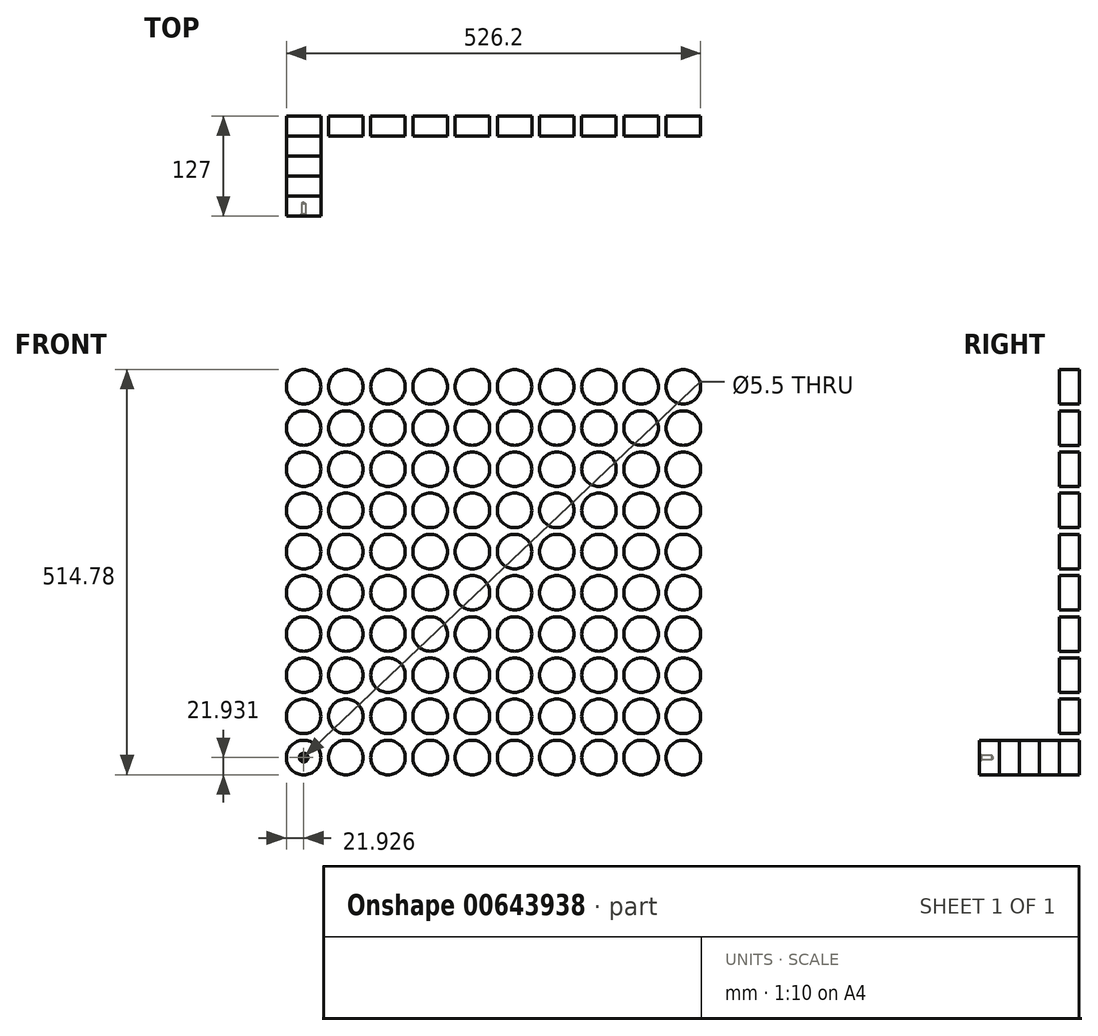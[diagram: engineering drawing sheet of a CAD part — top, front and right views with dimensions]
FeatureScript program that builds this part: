
annotation { "Feature Type Name" : "Feature", "Feature Type Description" : "" }
export const myFeature = defineFeature(function(context is Context, id is Id, definition is map)
    precondition{}
    {
        {
            var Q0;
            Q0=qCreatedBy(makeId("Front.planeOp"),FACE);
            var sketch = newSketch(context, id + "F0", { "sketchPlane" : qUnion([Q0])});
            skCircle(sketch, "E0", {"center": v(-112.8, -47.45) * mm, "radius": 21.93 * mm});
            skCircle(sketch, "E1.0.1.0", {"center": v(-112.8, 4.88) * mm, "radius": 21.93 * mm});
            skCircle(sketch, "E1.0.2.0", {"center": v(-112.8, 57.2) * mm, "radius": 21.93 * mm});
            skCircle(sketch, "E1.0.3.0", {"center": v(-112.8, 109.52) * mm, "radius": 21.93 * mm});
            skCircle(sketch, "E1.0.4.0", {"center": v(-112.8, 161.85) * mm, "radius": 21.93 * mm});
            skCircle(sketch, "E1.0.5.0", {"center": v(-112.8, 214.17) * mm, "radius": 21.93 * mm});
            skCircle(sketch, "E1.0.6.0", {"center": v(-112.8, 266.5) * mm, "radius": 21.93 * mm});
            skCircle(sketch, "E1.0.7.0", {"center": v(-112.8, 318.82) * mm, "radius": 21.93 * mm});
            skCircle(sketch, "E1.0.8.0", {"center": v(-112.8, 371.14) * mm, "radius": 21.93 * mm});
            skCircle(sketch, "E1.0.9.0", {"center": v(-112.8, 423.47) * mm, "radius": 21.93 * mm});
            skCircle(sketch, "E1.1.0.0", {"center": v(-59.2, -47.45) * mm, "radius": 21.93 * mm});
            skCircle(sketch, "E1.1.1.0", {"center": v(-59.2, 4.88) * mm, "radius": 21.93 * mm});
            skCircle(sketch, "E1.1.2.0", {"center": v(-59.2, 57.2) * mm, "radius": 21.93 * mm});
            skCircle(sketch, "E1.1.3.0", {"center": v(-59.2, 109.52) * mm, "radius": 21.93 * mm});
            skCircle(sketch, "E1.1.4.0", {"center": v(-59.2, 161.85) * mm, "radius": 21.93 * mm});
            skCircle(sketch, "E1.1.5.0", {"center": v(-59.2, 214.17) * mm, "radius": 21.93 * mm});
            skCircle(sketch, "E1.1.6.0", {"center": v(-59.2, 266.5) * mm, "radius": 21.93 * mm});
            skCircle(sketch, "E1.1.7.0", {"center": v(-59.2, 318.82) * mm, "radius": 21.93 * mm});
            skCircle(sketch, "E1.1.8.0", {"center": v(-59.2, 371.14) * mm, "radius": 21.93 * mm});
            skCircle(sketch, "E1.1.9.0", {"center": v(-59.2, 423.47) * mm, "radius": 21.93 * mm});
            skCircle(sketch, "E1.2.0.0", {"center": v(-5.62, -47.45) * mm, "radius": 21.93 * mm});
            skCircle(sketch, "E1.2.1.0", {"center": v(-5.62, 4.88) * mm, "radius": 21.93 * mm});
            skCircle(sketch, "E1.2.2.0", {"center": v(-5.62, 57.2) * mm, "radius": 21.93 * mm});
            skCircle(sketch, "E1.2.3.0", {"center": v(-5.62, 109.52) * mm, "radius": 21.93 * mm});
            skCircle(sketch, "E1.2.4.0", {"center": v(-5.62, 161.85) * mm, "radius": 21.93 * mm});
            skCircle(sketch, "E1.2.5.0", {"center": v(-5.62, 214.17) * mm, "radius": 21.93 * mm});
            skCircle(sketch, "E1.2.6.0", {"center": v(-5.62, 266.5) * mm, "radius": 21.93 * mm});
            skCircle(sketch, "E1.2.7.0", {"center": v(-5.62, 318.82) * mm, "radius": 21.93 * mm});
            skCircle(sketch, "E1.2.8.0", {"center": v(-5.62, 371.14) * mm, "radius": 21.93 * mm});
            skCircle(sketch, "E1.2.9.0", {"center": v(-5.62, 423.47) * mm, "radius": 21.93 * mm});
            skCircle(sketch, "E1.3.0.0", {"center": v(47.98, -47.45) * mm, "radius": 21.93 * mm});
            skCircle(sketch, "E1.3.1.0", {"center": v(47.98, 4.88) * mm, "radius": 21.93 * mm});
            skCircle(sketch, "E1.3.2.0", {"center": v(47.98, 57.2) * mm, "radius": 21.93 * mm});
            skCircle(sketch, "E1.3.3.0", {"center": v(47.98, 109.52) * mm, "radius": 21.93 * mm});
            skCircle(sketch, "E1.3.4.0", {"center": v(47.98, 161.85) * mm, "radius": 21.93 * mm});
            skCircle(sketch, "E1.3.5.0", {"center": v(47.98, 214.17) * mm, "radius": 21.93 * mm});
            skCircle(sketch, "E1.3.6.0", {"center": v(47.98, 266.5) * mm, "radius": 21.93 * mm});
            skCircle(sketch, "E1.3.7.0", {"center": v(47.98, 318.82) * mm, "radius": 21.93 * mm});
            skCircle(sketch, "E1.3.8.0", {"center": v(47.98, 371.14) * mm, "radius": 21.93 * mm});
            skCircle(sketch, "E1.3.9.0", {"center": v(47.98, 423.47) * mm, "radius": 21.93 * mm});
            skCircle(sketch, "E1.4.0.0", {"center": v(101.57, -47.45) * mm, "radius": 21.93 * mm});
            skCircle(sketch, "E1.4.1.0", {"center": v(101.57, 4.88) * mm, "radius": 21.93 * mm});
            skCircle(sketch, "E1.4.2.0", {"center": v(101.57, 57.2) * mm, "radius": 21.93 * mm});
            skCircle(sketch, "E1.4.3.0", {"center": v(101.57, 109.52) * mm, "radius": 21.93 * mm});
            skCircle(sketch, "E1.4.4.0", {"center": v(101.57, 161.85) * mm, "radius": 21.93 * mm});
            skCircle(sketch, "E1.4.5.0", {"center": v(101.57, 214.17) * mm, "radius": 21.93 * mm});
            skCircle(sketch, "E1.4.6.0", {"center": v(101.57, 266.5) * mm, "radius": 21.93 * mm});
            skCircle(sketch, "E1.4.7.0", {"center": v(101.57, 318.82) * mm, "radius": 21.93 * mm});
            skCircle(sketch, "E1.4.8.0", {"center": v(101.57, 371.14) * mm, "radius": 21.93 * mm});
            skCircle(sketch, "E1.4.9.0", {"center": v(101.57, 423.47) * mm, "radius": 21.93 * mm});
            skCircle(sketch, "E1.5.0.0", {"center": v(155.17, -47.45) * mm, "radius": 21.93 * mm});
            skCircle(sketch, "E1.5.1.0", {"center": v(155.17, 4.88) * mm, "radius": 21.93 * mm});
            skCircle(sketch, "E1.5.2.0", {"center": v(155.17, 57.2) * mm, "radius": 21.93 * mm});
            skCircle(sketch, "E1.5.3.0", {"center": v(155.17, 109.52) * mm, "radius": 21.93 * mm});
            skCircle(sketch, "E1.5.4.0", {"center": v(155.17, 161.85) * mm, "radius": 21.93 * mm});
            skCircle(sketch, "E1.5.5.0", {"center": v(155.17, 214.17) * mm, "radius": 21.93 * mm});
            skCircle(sketch, "E1.5.6.0", {"center": v(155.17, 266.5) * mm, "radius": 21.93 * mm});
            skCircle(sketch, "E1.5.7.0", {"center": v(155.17, 318.82) * mm, "radius": 21.93 * mm});
            skCircle(sketch, "E1.5.8.0", {"center": v(155.17, 371.14) * mm, "radius": 21.93 * mm});
            skCircle(sketch, "E1.5.9.0", {"center": v(155.17, 423.47) * mm, "radius": 21.93 * mm});
            skCircle(sketch, "E1.6.0.0", {"center": v(208.76, -47.45) * mm, "radius": 21.93 * mm});
            skCircle(sketch, "E1.6.1.0", {"center": v(208.76, 4.88) * mm, "radius": 21.93 * mm});
            skCircle(sketch, "E1.6.2.0", {"center": v(208.76, 57.2) * mm, "radius": 21.93 * mm});
            skCircle(sketch, "E1.6.3.0", {"center": v(208.76, 109.52) * mm, "radius": 21.93 * mm});
            skCircle(sketch, "E1.6.4.0", {"center": v(208.76, 161.85) * mm, "radius": 21.93 * mm});
            skCircle(sketch, "E1.6.5.0", {"center": v(208.76, 214.17) * mm, "radius": 21.93 * mm});
            skCircle(sketch, "E1.6.6.0", {"center": v(208.76, 266.5) * mm, "radius": 21.93 * mm});
            skCircle(sketch, "E1.6.7.0", {"center": v(208.76, 318.82) * mm, "radius": 21.93 * mm});
            skCircle(sketch, "E1.6.8.0", {"center": v(208.76, 371.14) * mm, "radius": 21.93 * mm});
            skCircle(sketch, "E1.6.9.0", {"center": v(208.76, 423.47) * mm, "radius": 21.93 * mm});
            skCircle(sketch, "E1.7.0.0", {"center": v(262.35, -47.45) * mm, "radius": 21.93 * mm});
            skCircle(sketch, "E1.7.1.0", {"center": v(262.35, 4.88) * mm, "radius": 21.93 * mm});
            skCircle(sketch, "E1.7.2.0", {"center": v(262.35, 57.2) * mm, "radius": 21.93 * mm});
            skCircle(sketch, "E1.7.3.0", {"center": v(262.35, 109.52) * mm, "radius": 21.93 * mm});
            skCircle(sketch, "E1.7.4.0", {"center": v(262.35, 161.85) * mm, "radius": 21.93 * mm});
            skCircle(sketch, "E1.7.5.0", {"center": v(262.35, 214.17) * mm, "radius": 21.93 * mm});
            skCircle(sketch, "E1.7.6.0", {"center": v(262.35, 266.5) * mm, "radius": 21.93 * mm});
            skCircle(sketch, "E1.7.7.0", {"center": v(262.35, 318.82) * mm, "radius": 21.93 * mm});
            skCircle(sketch, "E1.7.8.0", {"center": v(262.35, 371.14) * mm, "radius": 21.93 * mm});
            skCircle(sketch, "E1.7.9.0", {"center": v(262.35, 423.47) * mm, "radius": 21.93 * mm});
            skCircle(sketch, "E1.8.0.0", {"center": v(315.95, -47.45) * mm, "radius": 21.93 * mm});
            skCircle(sketch, "E1.8.1.0", {"center": v(315.95, 4.88) * mm, "radius": 21.93 * mm});
            skCircle(sketch, "E1.8.2.0", {"center": v(315.95, 57.2) * mm, "radius": 21.93 * mm});
            skCircle(sketch, "E1.8.3.0", {"center": v(315.95, 109.52) * mm, "radius": 21.93 * mm});
            skCircle(sketch, "E1.8.4.0", {"center": v(315.95, 161.85) * mm, "radius": 21.93 * mm});
            skCircle(sketch, "E1.8.5.0", {"center": v(315.95, 214.17) * mm, "radius": 21.93 * mm});
            skCircle(sketch, "E1.8.6.0", {"center": v(315.95, 266.5) * mm, "radius": 21.93 * mm});
            skCircle(sketch, "E1.8.7.0", {"center": v(315.95, 318.82) * mm, "radius": 21.93 * mm});
            skCircle(sketch, "E1.8.8.0", {"center": v(315.95, 371.14) * mm, "radius": 21.93 * mm});
            skCircle(sketch, "E1.8.9.0", {"center": v(315.95, 423.47) * mm, "radius": 21.93 * mm});
            skCircle(sketch, "E1.9.0.0", {"center": v(369.54, -47.45) * mm, "radius": 21.93 * mm});
            skCircle(sketch, "E1.9.1.0", {"center": v(369.54, 4.88) * mm, "radius": 21.93 * mm});
            skCircle(sketch, "E1.9.2.0", {"center": v(369.54, 57.2) * mm, "radius": 21.93 * mm});
            skCircle(sketch, "E1.9.3.0", {"center": v(369.54, 109.52) * mm, "radius": 21.93 * mm});
            skCircle(sketch, "E1.9.4.0", {"center": v(369.54, 161.85) * mm, "radius": 21.93 * mm});
            skCircle(sketch, "E1.9.5.0", {"center": v(369.54, 214.17) * mm, "radius": 21.93 * mm});
            skCircle(sketch, "E1.9.6.0", {"center": v(369.54, 266.5) * mm, "radius": 21.93 * mm});
            skCircle(sketch, "E1.9.7.0", {"center": v(369.54, 318.82) * mm, "radius": 21.93 * mm});
            skCircle(sketch, "E1.9.8.0", {"center": v(369.54, 371.14) * mm, "radius": 21.93 * mm});
            skCircle(sketch, "E1.9.9.0", {"center": v(369.54, 423.47) * mm, "radius": 21.93 * mm});
            skLineSegment(sketch, "E1.direction1", {"start": v(-112.8, -47.45) * mm, "end": v(-59.2, -47.45) * mm, "construction": true});
            skLineSegment(sketch, "E1.direction2", {"start": v(-112.8, -47.45) * mm, "end": v(-112.8, 4.88) * mm, "construction": true});
            skSolve(sketch);
        }
        {
            var Q0;
            Q0 = qSketchRegion(id + "F0", true);
            extrude(context, id + "F1", {"entities" : qUnion([Q0]), "depth" : 25.4 * mm, "offsetDistance" : 25.4 * mm});
        }
        {
            var Q0;
            Q0=makeQuery(id+"F1.opExtrude","CAP_FACE",FACE,{"disambiguationData":[OSD([sQuery(id+"F0.wireOp",EDGE,"E0")])],"isStart":false});
            extrude(context, id + "F2", {"entities" : qUnion([Q0]), "depth" : 25.4 * mm, "offsetDistance" : 25.4 * mm});
        }
        {
            var Q0;
            Q0=makeQuery(id+"F2.opExtrude","CAP_FACE",FACE,{"disambiguationData":[OSD([sQuery(id+"F0.wireOp",EDGE,"E0")])],"isStart":false});
            extrude(context, id + "F3", {"entities" : qUnion([Q0]), "depth" : 25.4 * mm, "offsetDistance" : 25.4 * mm});
        }
        {
            var Q0;
            Q0=makeQuery(id+"F3.opExtrude","CAP_FACE",FACE,{"disambiguationData":[OSD([sQuery(id+"F0.wireOp",EDGE,"E0")])],"isStart":false});
            extrude(context, id + "F4", {"entities" : qUnion([Q0]), "depth" : 25.4 * mm, "offsetDistance" : 25.4 * mm});
        }
        {
            var Q0;
            Q0=makeQuery(id+"F4.opExtrude","CAP_FACE",FACE,{"disambiguationData":[OSD([sQuery(id+"F0.wireOp",EDGE,"E0")])],"isStart":false});
            extrude(context, id + "F5", {"entities" : qUnion([Q0]), "depth" : 25.4 * mm, "offsetDistance" : 25.4 * mm});
        }
        {
            var Q0;
            Q0=makeQuery(id+"F5.opExtrude","CAP_FACE",FACE,{"disambiguationData":[OSD([sQuery(id+"F0.wireOp",EDGE,"E0")])],"isStart":false});
            var sketch = newSketch(context, id + "F6", { "sketchPlane" : qUnion([Q0])});
            skPoint(sketch, "E2", {"position": v(-112.8, -47.45) * mm});
            skSolve(sketch);
        }
        {
            var Q0;
            Q0=sQuery(id+"F6.wireOp",VERTEX,"E2");
            var Q1;
            Q1=makeQuery(id+"F4.opExtrude","SWEPT_BODY",BODY,{"disambiguationData":[OSD([sQuery(id+"F0.wireOp",EDGE,"E0")])]});
            var Q2;
            Q2=makeQuery(id+"F5.opExtrude","SWEPT_BODY",BODY,{"disambiguationData":[OSD([sQuery(id+"F0.wireOp",EDGE,"E0")])]});
            hole(context, id + "F7", {"style" : HoleStyle.C_SINK, "endStyle" : HoleEndStyle.BLIND, "standardTappedOrClearance" : lookupTablePath({ "standard" : "ISO", "fit" : "Normal", "size" : "M5", "type" : "Clearance" }), "standardBlindInLast" : lookupTablePath({ "fit" : "Standard", "standard" : "ISO", "size" : "M5", "type" : "Clearance" }), "holeDiameter" : 5.5 * mm, "cSinkDiameter" : 11.2 * mm, "cSinkAngle" : 90 * degree, "majorDiameter" : 3.17 * mm, "holeDepth" : 15.86 * mm, "isTappedThrough" : true, "tappedDepth" : 13.95 * mm, "tapClearance" : 3, "locations" : qUnion([Q0]), "scope" : qUnion([Q1, Q2])});
        }
    });
